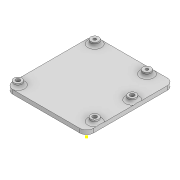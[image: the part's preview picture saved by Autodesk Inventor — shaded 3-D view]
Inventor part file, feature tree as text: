
AUTODESK INVENTOR PART (.ipt)
format: ipt  version: 2022 (Build 260153000, 153)  size: 284,160 bytes
history: native  units: mm
features: sketch x5, extrude x5, fillet x3, thicken_offset x2, chamfer x1, projected_geometry x1
ambient origin geometry x8: Origin, YZ Plane, XZ Plane, XY Plane, X Axis, Y Axis, Z Axis, Center Point
bodies: Solid1 (feature_tree)
feature tree (17):
  sketch  "Sketch1"  dims[d0=60.0mm d1=65.0mm]
  extrude  "Extrusion1"  Depth=60.0mm
  extrude  "Extrusion2"  Depth=10.0mm
  fillet  "Fillet1"  Radius=10.0mm
  extrude  "Extrusion3"  Depth=4.0mm
  extrude  "Extrusion4"  Depth=52.07mm
  thicken_offset  "Thicken1"
  thicken_offset  "Thicken2"
  chamfer  "Chamfer1"  Distance=27.94mm
  fillet  "Fillet2"  Radius=6.0mm
  fillet  "Fillet3"  Radius=6.0mm
  sketch  "Sketch4"  dims[d9=3.1mm d10=52.07mm]
  extrude  "Extrusion5"  Depth=3.0mm
  sketch  "Sketch2"  dims[d2=3.0mm d3=0.0mm d4=3.1mm d5=10.0mm]
  sketch  "Sketch3"  dims[d6=3.1mm d8=4.0mm]
  sketch  "Sketch5"  dims[d11=5.08mm d12=27.94mm d13=6.0mm d14=6.0mm d15=6.0mm d16=6.0mm d17=0.0mm d18=2.1mm d19=60.0mm d20=54.0mm d21=6.0mm d22=2.1mm d23=6.0mm d24=38.862mm d25=2.0mm d26=3.0mm d28=18.0mm d29=18.0mm d30=3.0mm d31=3.0mm d32=8.0mm d33=0.0mm d34=3.1mm d35=3.1mm d36=4.5mm d37=4.5mm d38=4.3mm d39=4.3mm d40=10.0mm d41=0.0mm d42=0.15mm d43=0.2mm d44=0.15mm d45=0.2mm d46=8.0mm d47=2.0mm d48=45.0deg d49=5.0mm d50=1.0mm d54=15.6mm d55=5.6mm d56=5.6mm d57=1.5mm d58=1.5mm d59=3.0mm d60=0.0mm]
  projected_geometry  "Projected Loop1"
